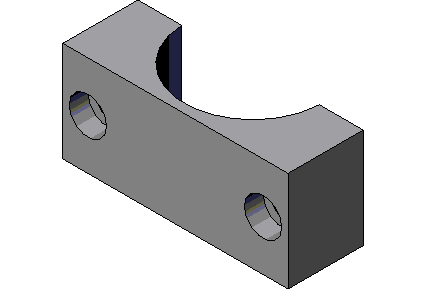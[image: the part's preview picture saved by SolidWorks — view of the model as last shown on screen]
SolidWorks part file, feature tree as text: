
SOLIDWORKS PART (.sldprt)
format: sldprt  version: not decoded by parser v0  size: 183,808 bytes
history: native  units: mm
features: sketch x4, extrude x1, cut_extrude x1, hole x1 (+10 scaffold rows collapsed)
feature tree (17):
  scaffold x10  (default folders/planes/origin — collapsed)
  sketch  "Sketch1"  dims[D1=57.15mm D2=19.05mm]
  extrude  "Extrude1"  Depth=25.4mm
  sketch  "Sketch2"  dims[D1=34.925mm D2=0.635mm]
  cut_extrude  "Cut-Extrude1"  [1 undecoded]
  hole  "CBORE for #10 Socket Head Cap Screw1"  Diameter=4.9784mm Depth=19.05mm
  sketch  "Sketch4"  dims[D1=44.45mm]
  sketch  "Sketch3"  dims[hole-wizard template sketch: 42 standard entries collapsed; hole parameters kept: c12.Thru Hole Depth=19.05mm c12.C'Bore Dia.=9.525mm c12.C'Bore Depth=4.826mm]
decode coverage: 6 of 7 modeling features carry decoded parameters
note: ~ marks probable driven/reference dimensions
note: 1 parameter value undecoded
note: suppression state not decoded; provenance and decode notes live in map.json
